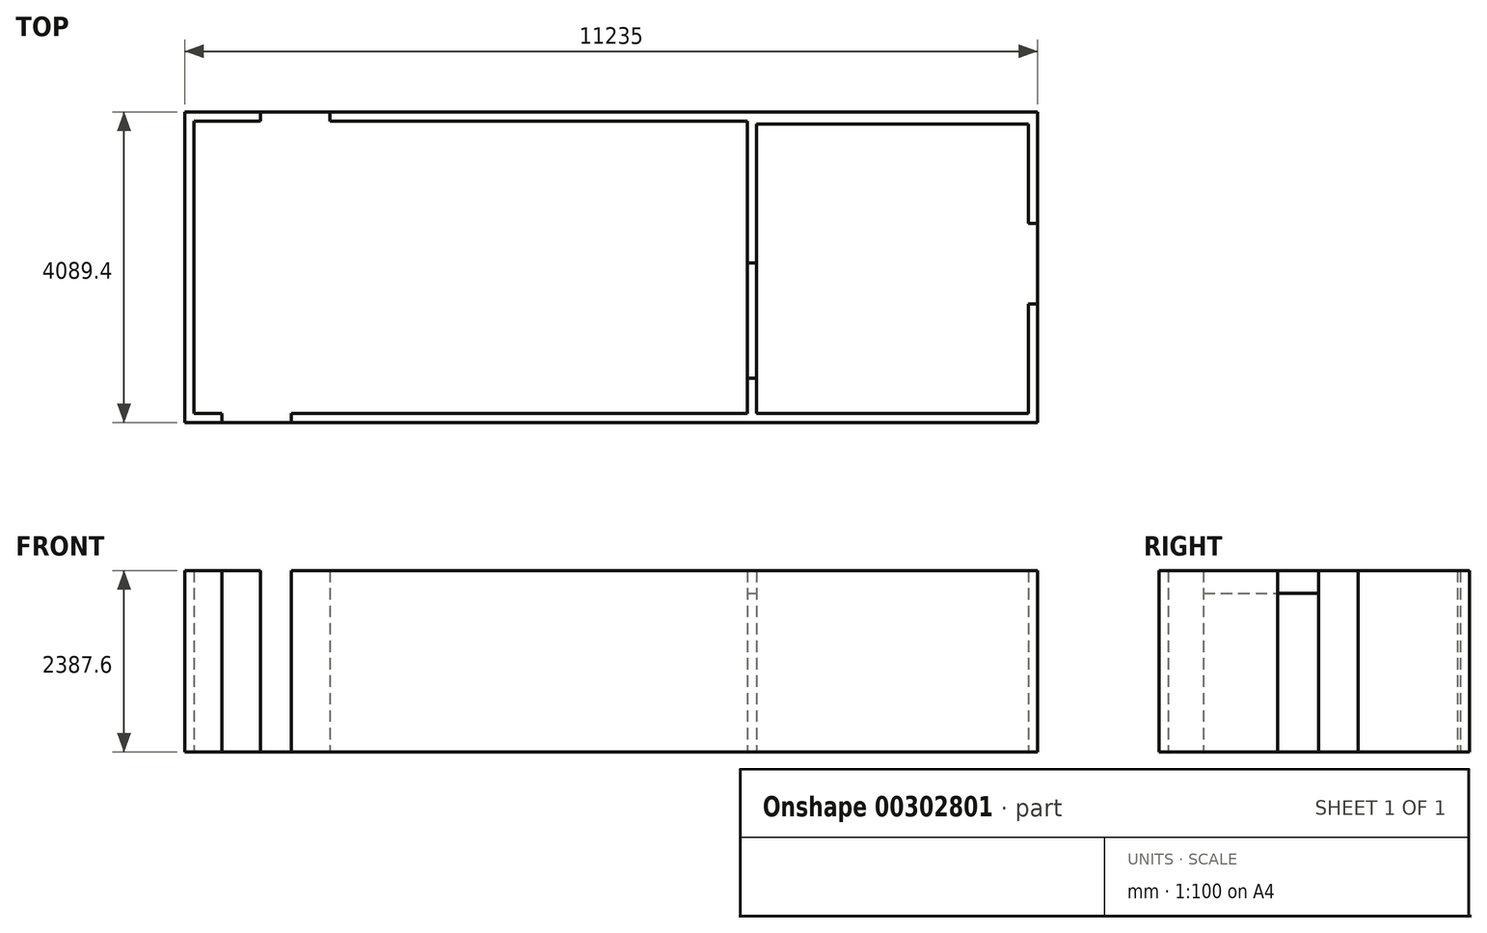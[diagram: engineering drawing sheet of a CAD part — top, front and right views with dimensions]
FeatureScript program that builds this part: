
annotation { "Feature Type Name" : "Feature", "Feature Type Description" : "" }
export const myFeature = defineFeature(function(context is Context, id is Id, definition is map)
    precondition{}
    {
        {
            var Q0;
            Q0=qCreatedBy(makeId("Top.planeOp"),FACE);
            var sketch = newSketch(context, id + "F0", { "sketchPlane" : qUnion([Q0])});
            skLineSegment(sketch, "E0", {"start": v(1498.49, 1242.53) * mm, "end": v(2374.79, 1242.53) * mm});
            skLineSegment(sketch, "E1", {"start": v(8790.07, 1242.53) * mm, "end": v(8790.07, -624.37) * mm});
            skLineSegment(sketch, "E2", {"start": v(8790.07, -624.37) * mm, "end": v(8910.72, -624.37) * mm});
            skLineSegment(sketch, "E3", {"start": v(8910.72, -624.37) * mm, "end": v(8910.72, 1204.43) * mm});
            skLineSegment(sketch, "E4", {"start": v(8910.72, 1204.43) * mm, "end": v(12492.12, 1204.43) * mm});
            skLineSegment(sketch, "E5", {"start": v(12492.12, 1204.43) * mm, "end": v(12492.12, -103.67) * mm});
            skLineSegment(sketch, "E6", {"start": v(12492.12, -2605.57) * mm, "end": v(8910.72, -2605.57) * mm});
            skLineSegment(sketch, "E7", {"start": v(8910.72, -2605.57) * mm, "end": v(8910.72, -2142.02) * mm});
            skLineSegment(sketch, "E8", {"start": v(8910.72, -2142.02) * mm, "end": v(8790.07, -2142.02) * mm});
            skLineSegment(sketch, "E9", {"start": v(8790.07, -2142.02) * mm, "end": v(8790.07, -2605.57) * mm});
            skLineSegment(sketch, "E10", {"start": v(8790.07, -2605.57) * mm, "end": v(2781.19, -2605.57) * mm});
            skLineSegment(sketch, "E11", {"start": v(1498.49, -2605.57) * mm, "end": v(1498.49, 1242.53) * mm});
            skPoint(sketch, "E12", {"position": v(1866.79, -2605.57) * mm});
            skPoint(sketch, "E13", {"position": v(2781.19, -2605.57) * mm});
            skLineSegment(sketch, "E14.trimOffspring", {"start": v(1866.79, -2605.57) * mm, "end": v(1498.49, -2605.57) * mm});
            skPoint(sketch, "E15", {"position": v(12492.12, 505.93) * mm});
            skPoint(sketch, "E16", {"position": v(12492.12, -103.67) * mm});
            skPoint(sketch, "E17", {"position": v(12492.12, -1164.12) * mm});
            skPoint(sketch, "E18", {"position": v(2374.79, 1242.53) * mm});
            skPoint(sketch, "E19", {"position": v(3289.19, 1242.53) * mm});
            skLineSegment(sketch, "E20.trimOffspring", {"start": v(12492.12, -1164.12) * mm, "end": v(12492.12, -2605.57) * mm});
            skLineSegment(sketch, "E21.trimOffspring", {"start": v(3289.19, 1242.53) * mm, "end": v(8790.07, 1242.53) * mm});
            skLineSegment(sketch, "E22", {"start": v(2374.79, 1363.18) * mm, "end": v(1377.84, 1363.18) * mm});
            skLineSegment(sketch, "E23", {"start": v(1377.84, 1363.18) * mm, "end": v(1377.84, -2726.22) * mm});
            skLineSegment(sketch, "E24", {"start": v(1377.84, -2726.22) * mm, "end": v(1866.79, -2726.22) * mm});
            skLineSegment(sketch, "E25", {"start": v(1866.79, -2726.22) * mm, "end": v(1866.79, -2605.57) * mm});
            skLineSegment(sketch, "E26", {"start": v(2374.79, 1242.53) * mm, "end": v(2374.79, 1363.18) * mm});
            skLineSegment(sketch, "E27", {"start": v(2781.19, -2605.57) * mm, "end": v(2781.19, -2726.22) * mm});
            skLineSegment(sketch, "E28", {"start": v(2781.19, -2726.22) * mm, "end": v(12612.77, -2726.22) * mm});
            skLineSegment(sketch, "E29", {"start": v(12612.77, -2726.22) * mm, "end": v(12612.77, -1164.12) * mm});
            skLineSegment(sketch, "E30", {"start": v(12612.77, -1164.12) * mm, "end": v(12492.12, -1164.12) * mm});
            skLineSegment(sketch, "E31", {"start": v(12492.12, -103.67) * mm, "end": v(12612.77, -103.67) * mm});
            skLineSegment(sketch, "E32", {"start": v(12612.77, -103.67) * mm, "end": v(12612.77, 1363.18) * mm});
            skLineSegment(sketch, "E33", {"start": v(12612.77, 1363.18) * mm, "end": v(3289.19, 1363.18) * mm});
            skLineSegment(sketch, "E34", {"start": v(3289.19, 1363.18) * mm, "end": v(3289.19, 1242.53) * mm});
            skSolve(sketch);
        }
        {
            var Q0;
            Q0=makeQuery(id+"F0.imprint","IMPRINT",FACE,{"disambiguationData":[TD([[makeQuery(id+"F0.imprint","IMPRINT",EDGE,{"derivedFrom":sQuery(id+"F0.wireOp",EDGE,"E0")}),1.0]])]});
            var Q1;
            Q1=makeQuery(id+"F0.imprint","IMPRINT",FACE,{"disambiguationData":[TD([[makeQuery(id+"F0.imprint","IMPRINT",EDGE,{"derivedFrom":sQuery(id+"F0.wireOp",EDGE,"E6")}),1.0]])]});
            var Q2;
            Q2=makeQuery(id+"F0.imprint","IMPRINT",FACE,{"disambiguationData":[TD([[makeQuery(id+"F0.imprint","IMPRINT",EDGE,{"derivedFrom":sQuery(id+"F0.wireOp",EDGE,"E1")}),1.0]])]});
            extrude(context, id + "F1", {"entities" : qUnion([Q0, Q1, Q2]), "depth" : 2387.6 * mm});
        }
        {
            var Q0;
            Q0=qCreatedBy(makeId("Top.planeOp"),FACE);
            var sketch = newSketch(context, id + "F2", { "sketchPlane" : qUnion([Q0])});
            skLineSegment(sketch, "E35.bottom", {"start": v(1377.8, -2725.98) * mm, "end": v(12612.7, -2725.98) * mm});
            skLineSegment(sketch, "E35.top", {"start": v(1377.8, 1363.12) * mm, "end": v(12612.7, 1363.12) * mm});
            skLineSegment(sketch, "E35.left", {"start": v(1377.8, -2725.98) * mm, "end": v(1377.8, 1363.12) * mm});
            skLineSegment(sketch, "E35.right", {"start": v(12612.7, -2725.98) * mm, "end": v(12612.7, 1363.12) * mm});
            skSolve(sketch);
        }
        {
            var Q0;
            Q0 = qSketchRegion(id + "F2", true);
            extrude(context, id + "F3", {"entities" : qUnion([Q0]), "depth" : 2.54 * mm});
        }
        {
            var Q0;
            Q0=makeQuery(id+"F1.opExtrude","SWEPT_FACE",FACE,{"disambiguationData":[OSD([sQuery(id+"F0.wireOp",EDGE,"E2")])]});
            var sketch = newSketch(context, id + "F4", { "sketchPlane" : qUnion([Q0])});
            skLineSegment(sketch, "E36.bottom", {"start": v(8790.07, 2387.6) * mm, "end": v(8910.72, 2387.6) * mm});
            skLineSegment(sketch, "E36.top", {"start": v(8790.07, 2089.15) * mm, "end": v(8910.72, 2089.15) * mm});
            skLineSegment(sketch, "E36.left", {"start": v(8790.07, 2387.6) * mm, "end": v(8790.07, 2089.15) * mm});
            skLineSegment(sketch, "E36.right", {"start": v(8910.72, 2387.6) * mm, "end": v(8910.72, 2089.15) * mm});
            skSolve(sketch);
        }
        {
            var Q0;
            Q0=makeQuery(id+"F4.imprint","IMPRINT",FACE,{"disambiguationData":[TD([[makeQuery(id+"F4.imprint","IMPRINT",EDGE,{"derivedFrom":sQuery(id+"F4.wireOp",EDGE,"E36.bottom")}),-1.0]])]});
            var Q1;
            Q1=makeQuery(id+"F1.opExtrude","SWEPT_FACE",FACE,{"disambiguationData":[OSD([sQuery(id+"F0.wireOp",EDGE,"E8")])]});
            extrude(context, id + "F5", {"entities" : qUnion([Q0]), "endBound" : BoundingType.UP_TO_SURFACE, "endBoundEntityFace" : qUnion([Q1]), "depth" : 25.4 * mm});
        }
    });
